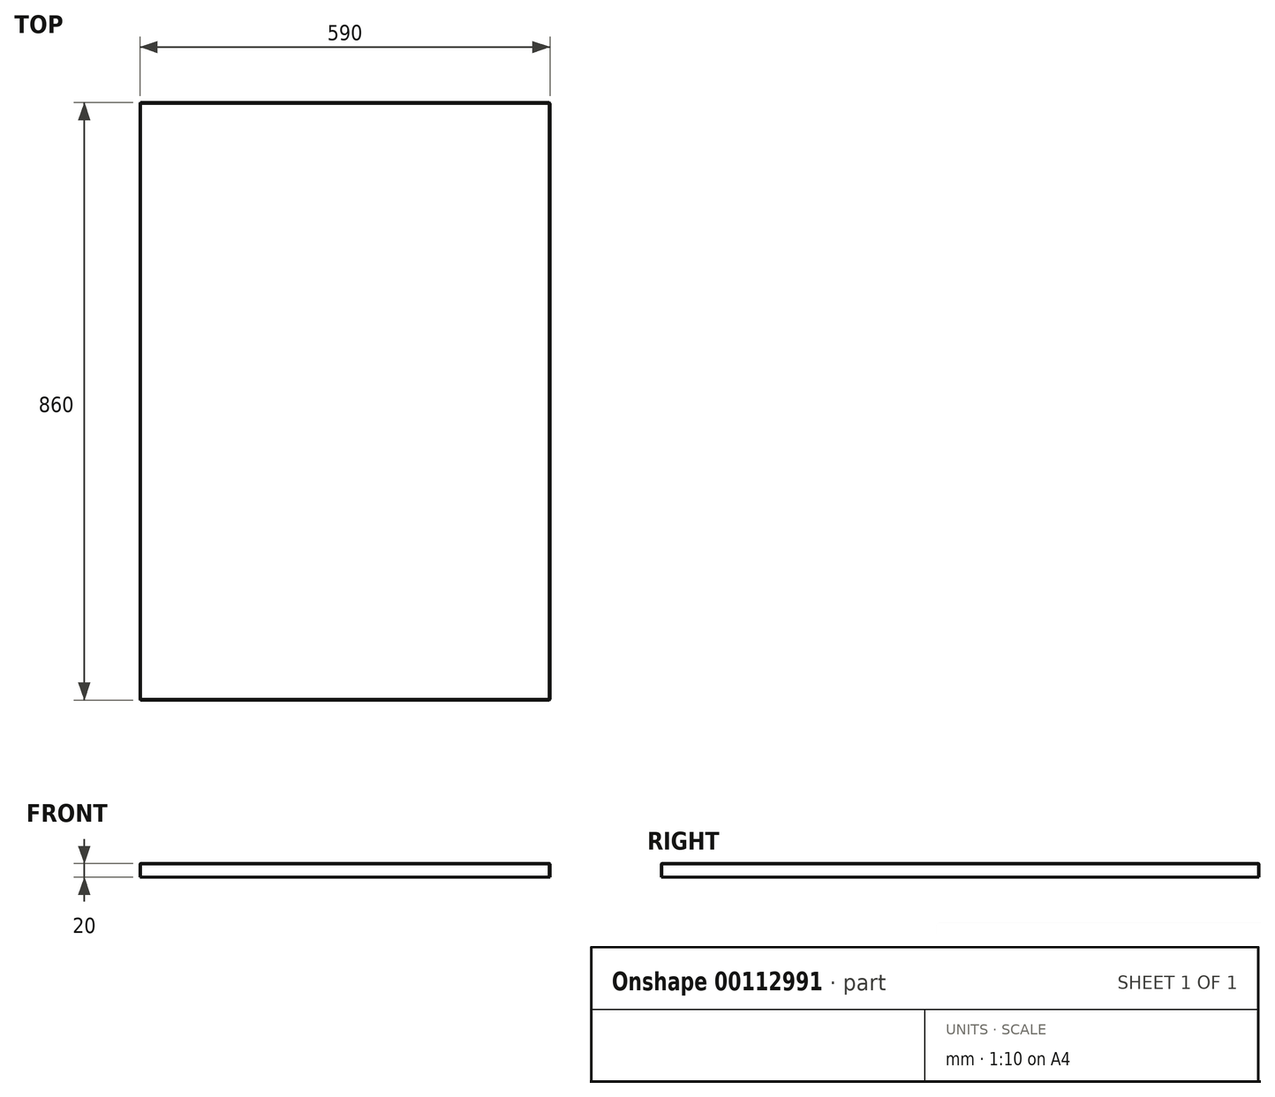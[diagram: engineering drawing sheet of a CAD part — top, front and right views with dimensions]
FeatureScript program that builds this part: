
annotation { "Feature Type Name" : "Feature", "Feature Type Description" : "" }
export const myFeature = defineFeature(function(context is Context, id is Id, definition is map)
    precondition{}
    {
        {
            var Q0;
            Q0=qCreatedBy(makeId("Front.planeOp"),FACE);
            var sketch = newSketch(context, id + "F0", { "sketchPlane" : qUnion([Q0])});
            skLineSegment(sketch, "E0.bottom", {"start": v(295, 0) * mm, "end": v(-295, 0) * mm});
            skLineSegment(sketch, "E0.top", {"start": v(295, 20) * mm, "end": v(-295, 20) * mm});
            skLineSegment(sketch, "E0.left", {"start": v(295, 0) * mm, "end": v(295, 20) * mm});
            skLineSegment(sketch, "E0.right", {"start": v(-295, 0) * mm, "end": v(-295, 20) * mm});
            skPoint(sketch, "E0.middle", {"position": v(0, 10) * mm});
            skSolve(sketch);
        }
        {
            var Q0;
            Q0=makeQuery(id+"F0.imprint","IMPRINT",FACE,{"disambiguationData":[TD([[makeQuery(id+"F0.imprint","IMPRINT",EDGE,{"derivedFrom":sQuery(id+"F0.wireOp",EDGE,"E0.bottom")}),-1.0]])]});
            extrude(context, id + "F1", {"entities" : qUnion([Q0]), "oppositeDirection" : true, "depth" : 860 * mm});
        }
        {
            var Q0;
            Q0=makeQuery(id+"F1.opExtrude","SWEPT_FACE",FACE,{"disambiguationData":[OSD([sQuery(id+"F0.wireOp",EDGE,"E0.top")])]});
            var Q1;
            Q1=makeQuery(id+"F1.opExtrude","CAP_EDGE",EDGE,{"disambiguationData":[OSD([sQuery(id+"F0.wireOp",EDGE,"E0.left")])],"isStart":true});
            var Q2;
            Q2=makeQuery(id+"F1.opExtrude","CAP_EDGE",EDGE,{"disambiguationData":[OSD([sQuery(id+"F0.wireOp",EDGE,"E0.left")])],"isStart":false});
            var Q3;
            Q3=makeQuery(id+"F1.opExtrude","CAP_EDGE",EDGE,{"disambiguationData":[OSD([sQuery(id+"F0.wireOp",EDGE,"E0.right")])],"isStart":true});
            var Q4;
            Q4=makeQuery(id+"F1.opExtrude","CAP_EDGE",EDGE,{"disambiguationData":[OSD([sQuery(id+"F0.wireOp",EDGE,"E0.right")])],"isStart":false});
            chamfer(context, id + "F2", {"entities" : qUnion([Q0, Q1, Q2, Q3, Q4]), "width" : 1 * mm, "tangentPropagation" : true});
        }
    });
